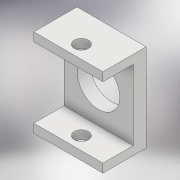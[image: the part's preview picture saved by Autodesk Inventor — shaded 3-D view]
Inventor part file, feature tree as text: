
AUTODESK INVENTOR PART (.ipt)
format: ipt  version: 2018.2 (Build 222227000, 227)  size: 137,728 bytes
history: native  units: mm
features: extrude x3, sketch x2
ambient origin geometry x8: Origin, YZ Plane, XZ Plane, XY Plane, X Axis, Y Axis, Z Axis, Center Point
bodies: Solid1 (feature_tree)
feature tree (5):
  sketch  "Sketch1"  dims[d0=9.8mm d1=2.0mm]
  extrude  "Extrusion1"  Depth=2.0mm
  extrude  "Extrusion2"  Depth=7.0mm
  extrude  "Extrusion3"  Depth=7.0mm
  sketch  "Sketch2"  dims[d2=16.0mm d3=8.0mm d4=0.15mm d5=0.15mm d6=16.0mm d7=2.0mm d8=2.0mm d9=3.0mm d10=0.0mm d11=7.0mm d12=0.0mm d13=3.3mm d14=3.0mm d15=7.0mm d16=0.0mm]
